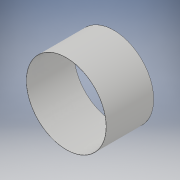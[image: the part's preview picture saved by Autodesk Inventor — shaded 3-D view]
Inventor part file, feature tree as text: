
AUTODESK INVENTOR PART (.ipt)
format: ipt  version: 2019 (Build 230136000, 136)  size: 103,936 bytes
history: native  units: mm
features: extrude x2, sketch x2
ambient origin geometry x8: Origin, YZ Plane, XZ Plane, XY Plane, X Axis, Y Axis, Z Axis, Center Point
bodies: Solid1 (feature_tree)
feature tree (4):
  extrude  "Extrusion1"  Depth=119.0mm TaperAngle=0.0deg
  extrude  "Extrusion2"  Depth=11.9mm TaperAngle=0.0deg
  sketch  "Sketch1"  dims[d0=200.7mm d1=119.0mm d2=0.0mm]
  sketch  "Sketch2"  dims[d3=199.7mm d4=11.9mm d5=0.0mm]
